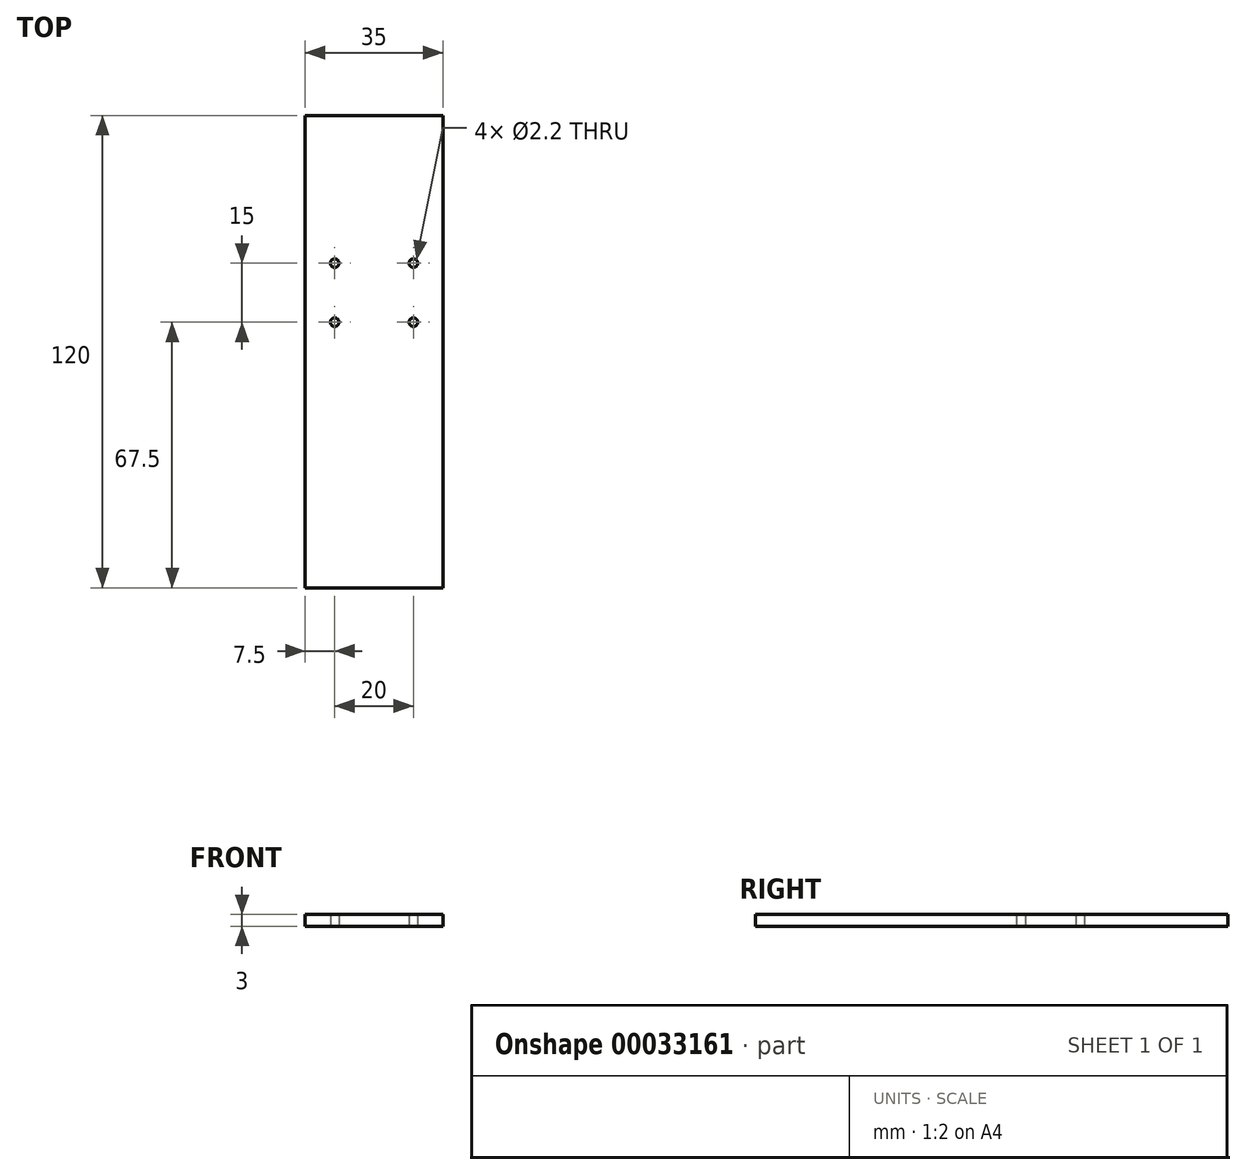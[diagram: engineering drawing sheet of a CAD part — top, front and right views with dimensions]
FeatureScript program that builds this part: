
annotation { "Feature Type Name" : "Feature", "Feature Type Description" : "" }
export const myFeature = defineFeature(function(context is Context, id is Id, definition is map)
    precondition{}
    {
        {
            var Q0;
            Q0=qCreatedBy(makeId("Top.planeOp"),FACE);
            var sketch = newSketch(context, id + "F0", { "sketchPlane" : qUnion([Q0])});
            skLineSegment(sketch, "E0.bottom", {"start": v(-17.5, 60) * mm, "end": v(17.5, 60) * mm});
            skLineSegment(sketch, "E0.top", {"start": v(-17.5, -60) * mm, "end": v(17.5, -60) * mm});
            skLineSegment(sketch, "E0.left", {"start": v(-17.5, 60) * mm, "end": v(-17.5, -60) * mm});
            skLineSegment(sketch, "E0.right", {"start": v(17.5, 60) * mm, "end": v(17.5, -60) * mm});
            skPoint(sketch, "E0.middle", {"position": v(0, 0) * mm});
            skLineSegment(sketch, "E1.bottom", {"start": v(-10, 22.5) * mm, "end": v(10, 22.5) * mm, "construction": true});
            skLineSegment(sketch, "E1.top", {"start": v(-10, 7.5) * mm, "end": v(10, 7.5) * mm, "construction": true});
            skLineSegment(sketch, "E1.left", {"start": v(-10, 22.5) * mm, "end": v(-10, 7.5) * mm, "construction": true});
            skLineSegment(sketch, "E1.right", {"start": v(10, 22.5) * mm, "end": v(10, 7.5) * mm, "construction": true});
            skPoint(sketch, "E1.middle", {"position": v(0, 15) * mm});
            skCircle(sketch, "E2", {"center": v(-10, 22.5) * mm, "radius": 1.1 * mm});
            skCircle(sketch, "E3", {"center": v(-10, 7.5) * mm, "radius": 1.1 * mm});
            skCircle(sketch, "E4", {"center": v(10, 22.5) * mm, "radius": 1.1 * mm});
            skCircle(sketch, "E5", {"center": v(10, 7.5) * mm, "radius": 1.1 * mm});
            skSolve(sketch);
        }
        {
            var Q0;
            Q0 = qSketchRegion(id + "F0", true);
            extrude(context, id + "F1", {"entities" : qUnion([Q0]), "depth" : 3 * mm});
        }
    });
